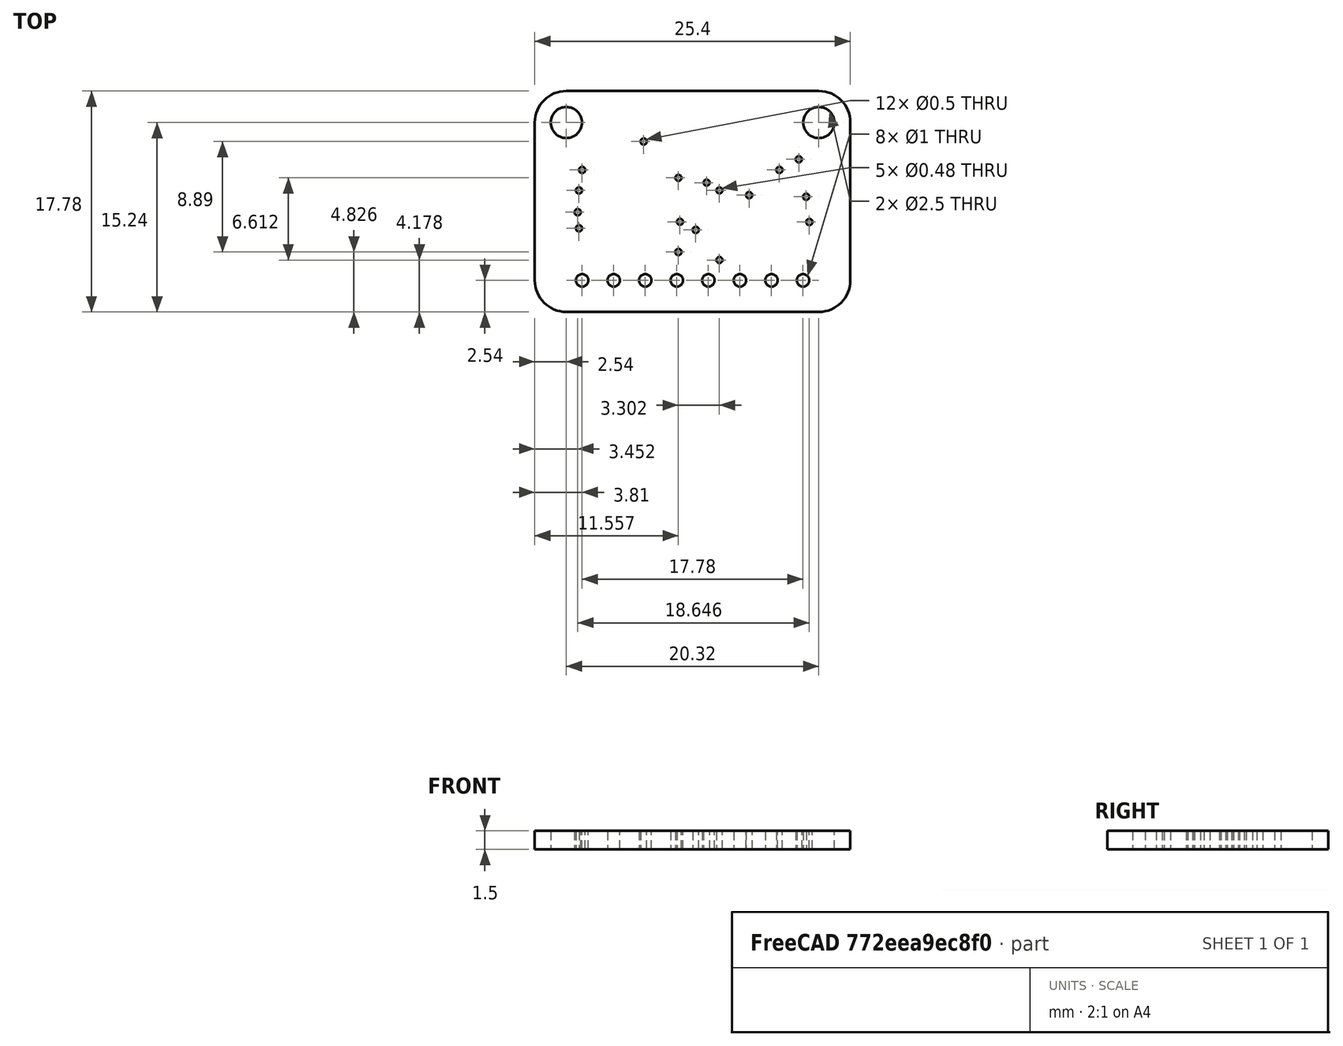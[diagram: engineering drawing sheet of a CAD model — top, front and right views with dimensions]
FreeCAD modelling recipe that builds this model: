
FCSTD DOCUMENT  (FreeCAD 0.20R29410 (Git))
Label: BMP388
License: All rights reserved
LicenseURL: http://en.wikipedia.org/wiki/All_rights_reserved
objects: App::DocumentObjectGroup×4, Sketcher::SketchObject×2, App::Part×1, Part::FeaturePython×1
note: 3 computed .brp shape members not serialized (recipe doc carries the construction recipe); baked Part::Feature solids carry a one-line shape summary decoded from their .brp

FEATURE [App::DocumentObjectGroup] Annotations
FEATURE [App::DocumentObjectGroup] Areas
FEATURE [App::DocumentObjectGroup] Layers
  Group = -> [Annotations,Areas]
FEATURE [Sketcher::SketchObject] PCB_Border
  FullyConstrained = false
  sketch-geometry (8):
    g0: LineSegment StartX=0 StartY=15.24 StartZ=0 EndX=0 EndY=2.54 EndZ=0
    g1: ArcOfCircle CenterX=2.54 CenterY=2.54 CenterZ=0 NormalX=0 NormalY=0 NormalZ=1 AngleXU=-3.14159 Radius=2.54 StartAngle=0 EndAngle=1.5708
    g2: LineSegment StartX=2.54 StartY=0 StartZ=0 EndX=22.86 EndY=0 EndZ=0
    g3: ArcOfCircle CenterX=22.86 CenterY=2.54 CenterZ=0 NormalX=0 NormalY=0 NormalZ=1 AngleXU=-1.5708 Radius=2.54 StartAngle=0 EndAngle=1.5708
    g4: LineSegment StartX=25.4 StartY=2.54 StartZ=0 EndX=25.4 EndY=15.24 EndZ=0
    g5: ArcOfCircle CenterX=22.86 CenterY=15.24 CenterZ=0 NormalX=0 NormalY=0 NormalZ=1 AngleXU=7e-16 Radius=2.54 StartAngle=0 EndAngle=1.5708
    g6: LineSegment StartX=22.86 StartY=17.78 StartZ=0 EndX=2.54 EndY=17.78 EndZ=0
    g7: ArcOfCircle CenterX=2.54 CenterY=15.24 CenterZ=0 NormalX=0 NormalY=0 NormalZ=1 AngleXU=1.5708 Radius=2.54 StartAngle=0 EndAngle=1.5708
FEATURE [Sketcher::SketchObject] PCB_Holes
  FullyConstrained = false
  sketch-geometry (27):
    g0: Circle CenterX=3.81 CenterY=11.43 CenterZ=0 NormalX=0 NormalY=0 NormalZ=1 AngleXU=0 Radius=0.251
    g1: Circle CenterX=22.098 CenterY=7.239 CenterZ=0 NormalX=0 NormalY=0 NormalZ=1 AngleXU=0 Radius=0.251
    g2: Circle CenterX=8.763 CenterY=13.716 CenterZ=0 NormalX=0 NormalY=0 NormalZ=1 AngleXU=0 Radius=0.251
    g3: Circle CenterX=12.954 CenterY=6.604 CenterZ=0 NormalX=0 NormalY=0 NormalZ=1 AngleXU=0 Radius=0.251
    g4: Circle CenterX=19.685 CenterY=11.43 CenterZ=0 NormalX=0 NormalY=0 NormalZ=1 AngleXU=0 Radius=0.251
    g5: Circle CenterX=11.684 CenterY=7.2517 CenterZ=0 NormalX=0 NormalY=0 NormalZ=1 AngleXU=0 Radius=0.2423
    g6: Circle CenterX=13.8303 CenterY=10.4013 CenterZ=0 NormalX=0 NormalY=0 NormalZ=1 AngleXU=0 Radius=0.2423
    g7: Circle CenterX=14.859 CenterY=4.1783 CenterZ=0 NormalX=0 NormalY=0 NormalZ=1 AngleXU=0 Radius=0.2423
    g8: Circle CenterX=14.859 CenterY=9.779 CenterZ=0 NormalX=0 NormalY=0 NormalZ=1 AngleXU=0 Radius=0.2423
    g9: Circle CenterX=3.45161 CenterY=8.02361 CenterZ=0 NormalX=0 NormalY=0 NormalZ=1 AngleXU=0 Radius=0.251
    g10: Circle CenterX=21.844 CenterY=9.271 CenterZ=0 NormalX=0 NormalY=0 NormalZ=1 AngleXU=0 Radius=0.251
    g11: Circle CenterX=17.253 CenterY=9.398 CenterZ=0 NormalX=0 NormalY=0 NormalZ=1 AngleXU=0 Radius=0.251
    g12: Circle CenterX=3.556 CenterY=6.731 CenterZ=0 NormalX=0 NormalY=0 NormalZ=1 AngleXU=0 Radius=0.251
    g13: Circle CenterX=11.557 CenterY=4.826 CenterZ=0 NormalX=0 NormalY=0 NormalZ=1 AngleXU=0 Radius=0.251
    g14: Circle CenterX=11.557 CenterY=10.7903 CenterZ=0 NormalX=0 NormalY=0 NormalZ=1 AngleXU=0 Radius=0.2423
    g15: Circle CenterX=21.248 CenterY=12.28 CenterZ=0 NormalX=0 NormalY=0 NormalZ=1 AngleXU=0 Radius=0.251
    g16: Circle CenterX=3.556 CenterY=9.779 CenterZ=0 NormalX=0 NormalY=0 NormalZ=1 AngleXU=0 Radius=0.251
    g17: Circle CenterX=3.81 CenterY=2.54 CenterZ=0 NormalX=0 NormalY=0 NormalZ=1 AngleXU=0 Radius=0.501
    g18: Circle CenterX=6.35 CenterY=2.54 CenterZ=0 NormalX=0 NormalY=0 NormalZ=1 AngleXU=0 Radius=0.501
    g19: Circle CenterX=8.89 CenterY=2.54 CenterZ=0 NormalX=0 NormalY=0 NormalZ=1 AngleXU=0 Radius=0.501
    g20: Circle CenterX=11.43 CenterY=2.54 CenterZ=0 NormalX=0 NormalY=0 NormalZ=1 AngleXU=0 Radius=0.501
    g21: Circle CenterX=13.97 CenterY=2.54 CenterZ=0 NormalX=0 NormalY=0 NormalZ=1 AngleXU=0 Radius=0.501
    g22: Circle CenterX=16.51 CenterY=2.54 CenterZ=0 NormalX=0 NormalY=0 NormalZ=1 AngleXU=0 Radius=0.501
    g23: Circle CenterX=19.05 CenterY=2.54 CenterZ=0 NormalX=0 NormalY=0 NormalZ=1 AngleXU=0 Radius=0.501
    g24: Circle CenterX=21.59 CenterY=2.54 CenterZ=0 NormalX=0 NormalY=0 NormalZ=1 AngleXU=0 Radius=0.501
    g25: Circle CenterX=2.54 CenterY=15.24 CenterZ=0 NormalX=0 NormalY=0 NormalZ=1 AngleXU=0 Radius=1.251
    g26: Circle CenterX=22.86 CenterY=15.24 CenterZ=0 NormalX=0 NormalY=0 NormalZ=1 AngleXU=0 Radius=1.251
FEATURE [App::Part] Adafruit_BMP388_QT_PCB  label="Adafruit BMP388 QT_PCB"
  Group = -> [Layers,PCB,Annotations,Areas,PCB_Border,Board,PCB_Holes]
  Origin = -> Origin
FEATURE [App::DocumentObjectGroup] PCB
  Group = -> [Board]
FEATURE [Part::FeaturePython] Board  # WARN: FeaturePython — macro-defined, semantics opaque (R4)
  AutoUpdate = true
  Border = -> PCB_Border
  Display = true
  Holes = -> PCB_Holes
  Parent = -> Adafruit_BMP388_QT_PCB
  Thickness = 1.5
